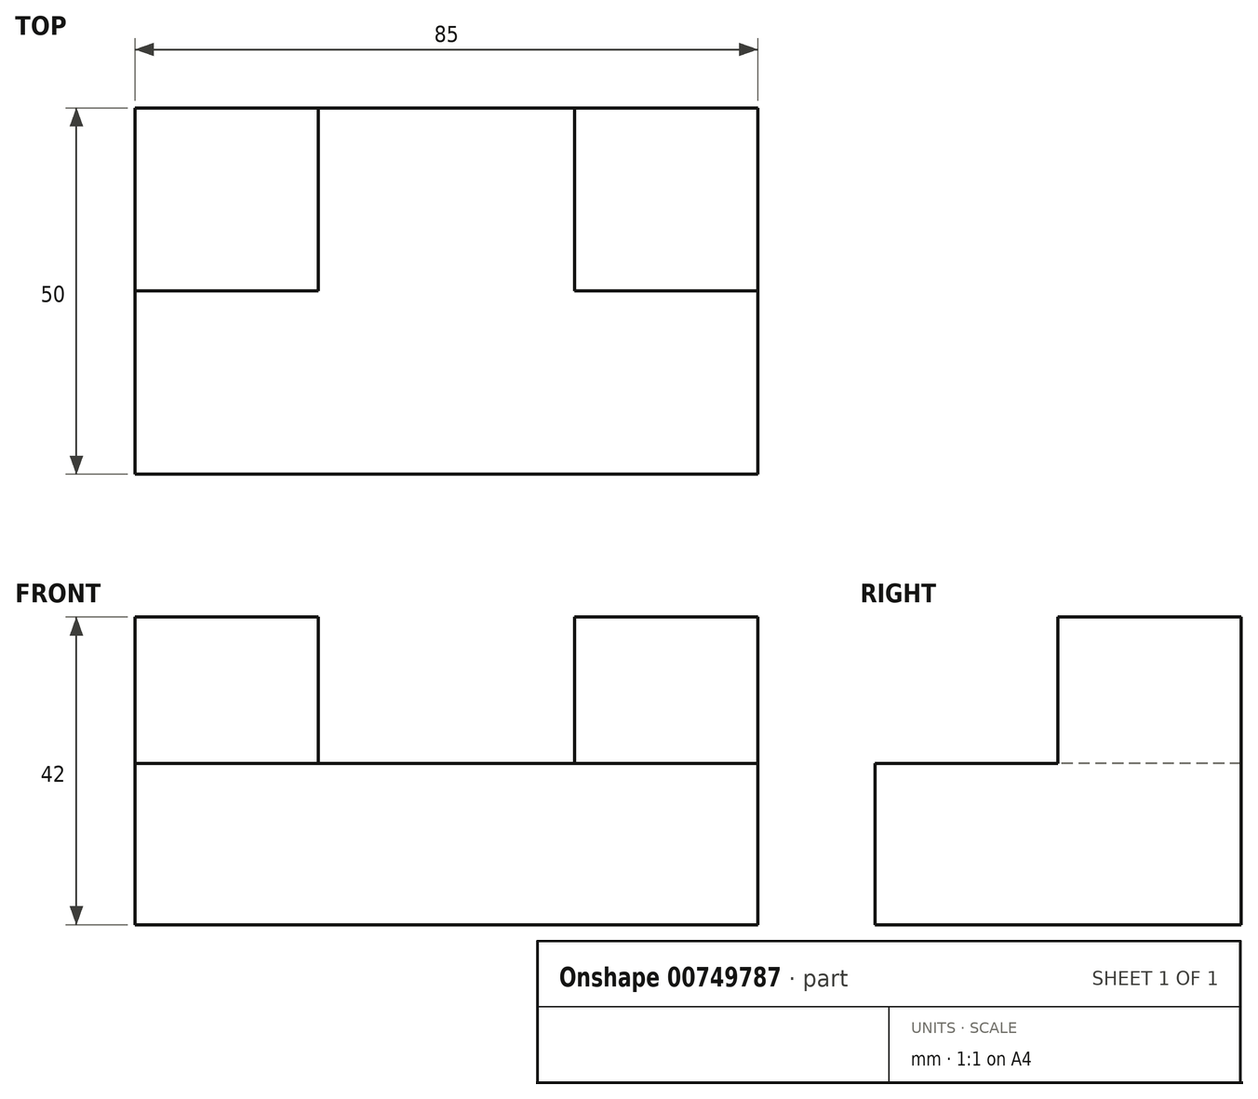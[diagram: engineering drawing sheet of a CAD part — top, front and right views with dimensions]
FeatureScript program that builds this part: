
annotation { "Feature Type Name" : "Feature", "Feature Type Description" : "" }
export const myFeature = defineFeature(function(context is Context, id is Id, definition is map)
    precondition{}
    {
        {
            var Q0;
            Q0=qCreatedBy(makeId("Top.planeOp"),FACE);
            var sketch = newSketch(context, id + "F0", { "sketchPlane" : qUnion([Q0])});
            skLineSegment(sketch, "E0.bottom", {"start": v(0, 0) * mm, "end": v(85, 0) * mm});
            skLineSegment(sketch, "E0.top", {"start": v(0, 50) * mm, "end": v(85, 50) * mm});
            skLineSegment(sketch, "E0.left", {"start": v(0, 0) * mm, "end": v(0, 50) * mm});
            skLineSegment(sketch, "E0.right", {"start": v(85, 0) * mm, "end": v(85, 50) * mm});
            skSolve(sketch);
        }
        {
            var Q0;
            Q0=makeQuery(id+"F0.imprint","IMPRINT",FACE,{"disambiguationData":[TD([[makeQuery(id+"F0.imprint","IMPRINT",EDGE,{"derivedFrom":sQuery(id+"F0.wireOp",EDGE,"E0.bottom")}),1.0]])]});
            extrude(context, id + "F1", {"entities" : qUnion([Q0]), "depth" : 42 * mm, "offsetDistance" : 25 * mm});
        }
        {
            var Q0;
            Q0=makeQuery(id+"F1.opExtrude","CAP_FACE",FACE,{"disambiguationData":[OSD([sQuery(id+"F0.wireOp",EDGE,"E0.bottom"),sQuery(id+"F0.wireOp",EDGE,"E0.top"),sQuery(id+"F0.wireOp",EDGE,"E0.left"),sQuery(id+"F0.wireOp",EDGE,"E0.right")])],"isStart":false});
            var sketch = newSketch(context, id + "F2", { "sketchPlane" : qUnion([Q0])});
            skLineSegment(sketch, "E1", {"start": v(0, 50) * mm, "end": v(25, 50) * mm});
            skLineSegment(sketch, "E2", {"start": v(25, 50) * mm, "end": v(25, 25) * mm});
            skLineSegment(sketch, "E3", {"start": v(25, 25) * mm, "end": v(0, 25) * mm});
            skLineSegment(sketch, "E4", {"start": v(0, 25) * mm, "end": v(0, 50) * mm});
            skLineSegment(sketch, "E5", {"start": v(85, 50) * mm, "end": v(85, 25) * mm});
            skLineSegment(sketch, "E6", {"start": v(85, 25) * mm, "end": v(60, 25) * mm});
            skLineSegment(sketch, "E7", {"start": v(60, 25) * mm, "end": v(60, 50) * mm});
            skLineSegment(sketch, "E8", {"start": v(60, 50) * mm, "end": v(85, 50) * mm});
            skLineSegment(sketch, "E9", {"start": v(25, 50) * mm, "end": v(60, 50) * mm});
            skLineSegment(sketch, "E10", {"start": v(60, 25) * mm, "end": v(25, 25) * mm});
            skLineSegment(sketch, "E11", {"start": v(0, 25) * mm, "end": v(0, 0) * mm});
            skLineSegment(sketch, "E12", {"start": v(0, 0) * mm, "end": v(85, 0) * mm});
            skLineSegment(sketch, "E13", {"start": v(85, 0) * mm, "end": v(85, 25) * mm});
            skSolve(sketch);
        }
        {
            var Q0;
            Q0=makeQuery(id+"F2.imprint","IMPRINT",FACE,{"disambiguationData":[TD([[makeQuery(id+"F2.imprint","IMPRINT",EDGE,{"derivedFrom":sQuery(id+"F2.wireOp",EDGE,"E2")}),1.0]])]});
            var Q1;
            Q1=makeQuery(id+"F2.imprint","IMPRINT",FACE,{"disambiguationData":[TD([[makeQuery(id+"F2.imprint","IMPRINT",EDGE,{"derivedFrom":sQuery(id+"F2.wireOp",EDGE,"E3")}),1.0]])]});
            extrude(context, id + "F3", {"entities" : qUnion([Q0, Q1]), "operationType" : NewBodyOperationType.REMOVE, "oppositeDirection" : true, "depth" : 20 * mm, "offsetDistance" : 25 * mm});
        }
    });
